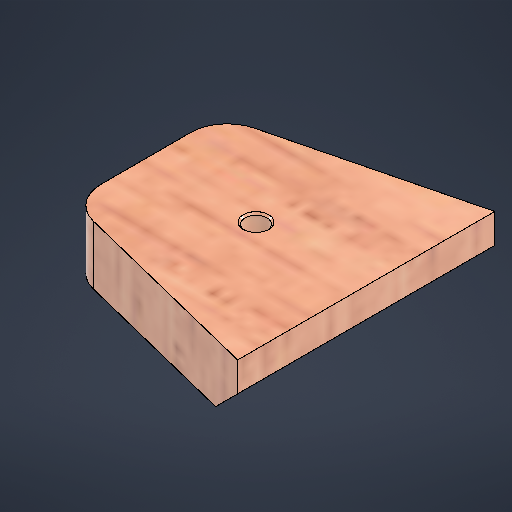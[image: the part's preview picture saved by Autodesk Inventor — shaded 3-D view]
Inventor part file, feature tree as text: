
AUTODESK INVENTOR PART (.ipt)
format: ipt  version: 2025.3 (Build 293356000, 356)  size: 282,112 bytes
history: native  units: mm
features: chamfer x2, sketch x1, extrude x1, hole x1, fillet x1
ambient origin geometry x8: Origin, YZ Plane, XZ Plane, XY Plane, X Axis, Y Axis, Z Axis, Center Point
bodies: Solid1 (feature_tree)
feature tree (6):
  sketch  "Sketch1"  dims[d1=30.0mm d2=35.0mm d3=8.0mm d4=0.0mm d5=3.0mm d6=8.0mm d7=3.5mm d8=6.8mm d9=90.0deg d10=8.0mm d11=20.594885mm d12=0.25mm d13=2.0mm d14=45.0deg d15=5.0mm d19=20.0mm d20=30.0mm d21=4.0mm d22=2.0mm d23=45.0deg]
  extrude  "Extrusion1"  Depth=30.0mm
  hole  "Hole1"  [1 undecoded]
  chamfer  "Chamfer1"  Distance=0.25mm Angle=45.0deg
  fillet  "Fillet1"  Radius=5.0mm
  chamfer  "Chamfer3"  Distance=20.0mm
note: 1 required parameter value undecoded (feature->parameter linkage not recoverable at this tier; creation-order binding heuristic only, values carry confidence <= 0.55)
